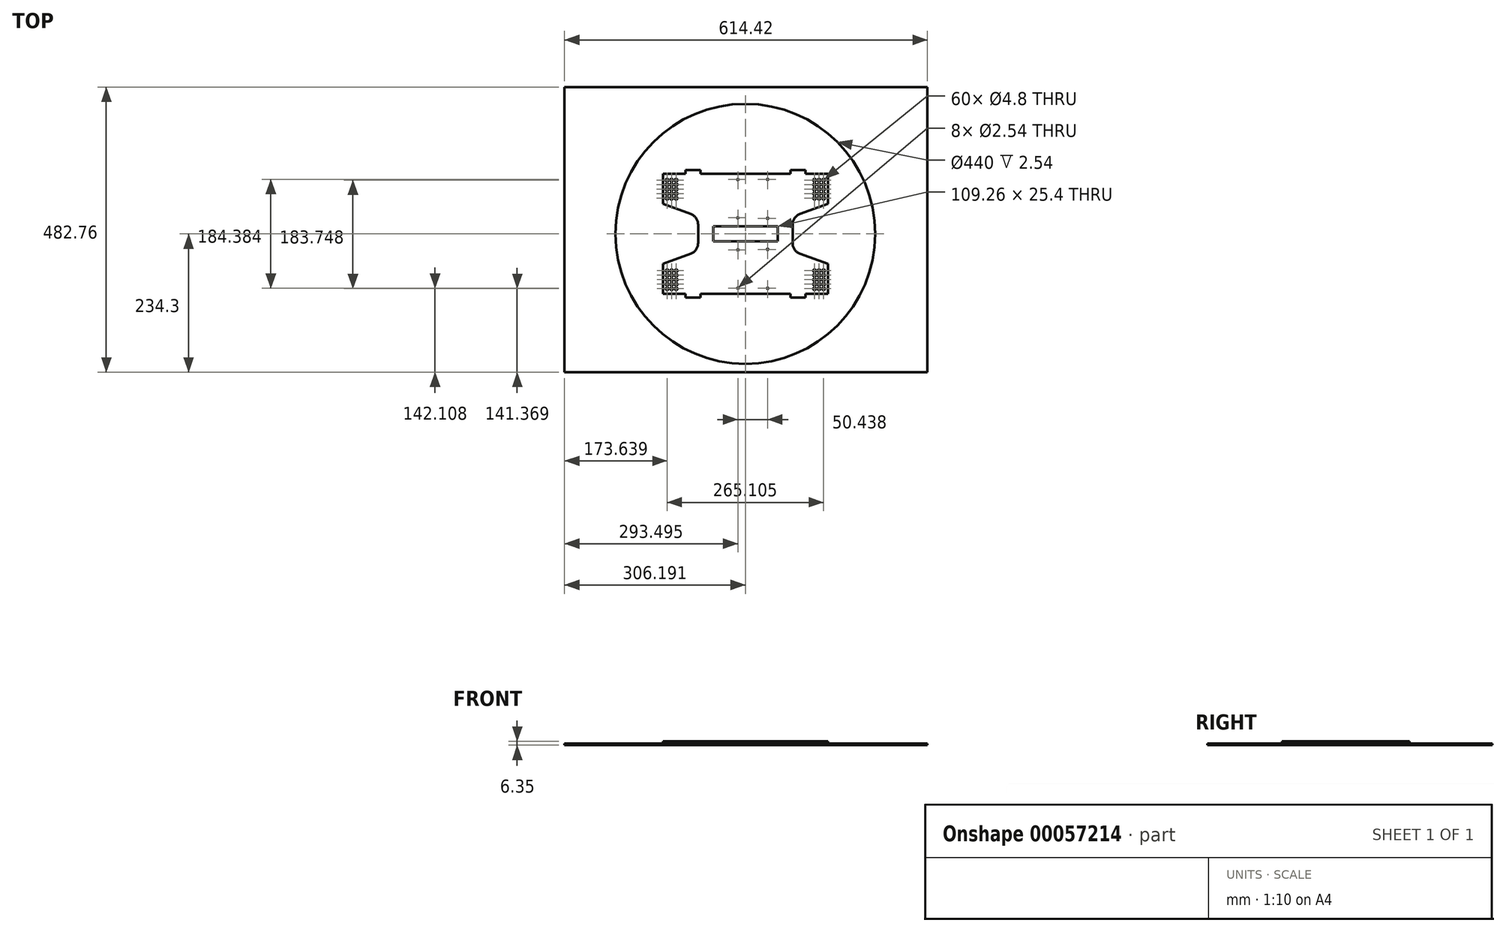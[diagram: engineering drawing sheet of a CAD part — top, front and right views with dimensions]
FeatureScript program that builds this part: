
annotation { "Feature Type Name" : "Feature", "Feature Type Description" : "" }
export const myFeature = defineFeature(function(context is Context, id is Id, definition is map)
    precondition{}
    {
        {
            var Q0;
            Q0=qCreatedBy(makeId("Top.planeOp"),FACE);
            var sketch = newSketch(context, id + "F0", { "sketchPlane" : qUnion([Q0])});
            skCircle(sketch, "E0", {"center": v(3.84, 0) * mm, "radius": 220 * mm});
            skLineSegment(sketch, "E1.bottom", {"start": v(-302.35, 248.46) * mm, "end": v(312.07, 248.46) * mm});
            skLineSegment(sketch, "E1.top", {"start": v(-302.35, -234.3) * mm, "end": v(312.07, -234.3) * mm});
            skLineSegment(sketch, "E1.left", {"start": v(-302.35, 248.46) * mm, "end": v(-302.35, -234.3) * mm});
            skLineSegment(sketch, "E1.right", {"start": v(312.07, 248.46) * mm, "end": v(312.07, -234.3) * mm});
            skSolve(sketch);
        }
        {
            var Q0;
            Q0=makeQuery(id+"F0.imprint","IMPRINT",FACE,{"disambiguationData":[TD([[makeQuery(id+"F0.imprint","IMPRINT",EDGE,{"derivedFrom":sQuery(id+"F0.wireOp",EDGE,"E0")}),1.0]])]});
            var sketch = newSketch(context, id + "F1", { "sketchPlane" : qUnion([Q0])});
            skLineSegment(sketch, "E2.bottom", {"start": v(-135.86, 101.6) * mm, "end": v(143.54, 101.6) * mm});
            skLineSegment(sketch, "E2.top", {"start": v(-135.86, -101.6) * mm, "end": v(143.54, -101.6) * mm});
            skLineSegment(sketch, "E2.left", {"start": v(-135.86, 101.6) * mm, "end": v(-135.86, -101.6) * mm});
            skLineSegment(sketch, "E2.right", {"start": v(143.54, 101.6) * mm, "end": v(143.54, -101.6) * mm});
            skLineSegment(sketch, "E3.bottom", {"start": v(-97.76, -101.6) * mm, "end": v(-72.36, -101.6) * mm});
            skLineSegment(sketch, "E3.top", {"start": v(-97.76, -107.95) * mm, "end": v(-72.36, -107.95) * mm});
            skLineSegment(sketch, "E3.left", {"start": v(-97.76, -101.6) * mm, "end": v(-97.76, -107.95) * mm});
            skLineSegment(sketch, "E3.right", {"start": v(-72.36, -101.6) * mm, "end": v(-72.36, -107.95) * mm});
            skLineSegment(sketch, "E4.bottom", {"start": v(105.44, -101.6) * mm, "end": v(80.04, -101.6) * mm});
            skLineSegment(sketch, "E4.top", {"start": v(105.44, -107.95) * mm, "end": v(80.04, -107.95) * mm});
            skLineSegment(sketch, "E4.left", {"start": v(105.44, -101.6) * mm, "end": v(105.44, -107.95) * mm});
            skLineSegment(sketch, "E4.right", {"start": v(80.04, -101.6) * mm, "end": v(80.04, -107.95) * mm});
            skLineSegment(sketch, "E5.MirrorCS", {"start": v(-97.76, 107.95) * mm, "end": v(-72.36, 107.95) * mm});
            skLineSegment(sketch, "E6.MirrorCS", {"start": v(-97.76, 101.6) * mm, "end": v(-72.36, 101.6) * mm});
            skLineSegment(sketch, "E7.MirrorCS", {"start": v(-97.76, 101.6) * mm, "end": v(-97.76, 107.95) * mm});
            skLineSegment(sketch, "E8.MirrorCS", {"start": v(-72.36, 101.6) * mm, "end": v(-72.36, 107.95) * mm});
            skLineSegment(sketch, "E9.MirrorCS", {"start": v(80.04, 101.6) * mm, "end": v(80.04, 107.95) * mm});
            skLineSegment(sketch, "E10.MirrorCS", {"start": v(105.44, 101.6) * mm, "end": v(105.44, 107.95) * mm});
            skLineSegment(sketch, "E11.MirrorCS", {"start": v(105.44, 107.95) * mm, "end": v(80.04, 107.95) * mm});
            skLineSegment(sketch, "E12.MirrorCS", {"start": v(105.44, 101.6) * mm, "end": v(80.04, 101.6) * mm});
            skLineSegment(sketch, "E13", {"start": v(95.83, 33.4) * mm, "end": v(143.54, 50.85) * mm});
            skLineSegment(sketch, "E14", {"start": v(95.78, -33.63) * mm, "end": v(95.83, 33.4) * mm});
            skLineSegment(sketch, "E15", {"start": v(143.54, -51.02) * mm, "end": v(95.78, -33.63) * mm});
            skLineSegment(sketch, "E16", {"start": v(-88.2, 33.27) * mm, "end": v(-135.86, 51.37) * mm});
            skLineSegment(sketch, "E17", {"start": v(-88.14, -33.49) * mm, "end": v(-88.2, 33.27) * mm});
            skLineSegment(sketch, "E18", {"start": v(-88.14, -33.49) * mm, "end": v(-135.86, -51.13) * mm});
            skSolve(sketch);
        }
        {
            var Q0;
            Q0=qSketchRegion(id+"F1",true);
            extrude(context, id + "F2", {"entities" : qUnion([Q0]), "depth" : 6.35 * mm});
        }
        {
            var Q0;
            Q0=makeQuery(id+"F0.imprint","IMPRINT",FACE,{"disambiguationData":[TD([[makeQuery(id+"F0.imprint","IMPRINT",EDGE,{"derivedFrom":sQuery(id+"F0.wireOp",EDGE,"E0")}),-1.0]])]});
            extrude(context, id + "F3", {"entities" : qUnion([Q0]), "depth" : 2.54 * mm});
        }
        {
            var Q0;
            Q0=makeQuery(id+"F2.opExtrude","CAP_FACE",FACE,{"disambiguationData":[OSD([sQuery(id+"F1.wireOp",EDGE,"E2.bottom"),sQuery(id+"F1.wireOp",EDGE,"E2.top"),sQuery(id+"F1.wireOp",EDGE,"E2.left"),sQuery(id+"F1.wireOp",EDGE,"E2.right"),sQuery(id+"F1.wireOp",EDGE,"E3.top"),sQuery(id+"F1.wireOp",EDGE,"E3.left"),sQuery(id+"F1.wireOp",EDGE,"E3.right"),sQuery(id+"F1.wireOp",EDGE,"E4.top"),sQuery(id+"F1.wireOp",EDGE,"E4.left"),sQuery(id+"F1.wireOp",EDGE,"E4.right"),sQuery(id+"F1.wireOp",EDGE,"E5.MirrorCS"),sQuery(id+"F1.wireOp",EDGE,"E7.MirrorCS"),sQuery(id+"F1.wireOp",EDGE,"E8.MirrorCS"),sQuery(id+"F1.wireOp",EDGE,"E9.MirrorCS"),sQuery(id+"F1.wireOp",EDGE,"E10.MirrorCS"),sQuery(id+"F1.wireOp",EDGE,"E11.MirrorCS")])],"isStart":false});
            var sketch = newSketch(context, id + "F4", { "sketchPlane" : qUnion([Q0])});
            skLineSegment(sketch, "E19", {"start": v(143.54, 50.8) * mm, "end": v(96.4, 33.64) * mm});
            skLineSegment(sketch, "E20", {"start": v(143.54, -50.8) * mm, "end": v(96.4, -33.64) * mm});
            skLineSegment(sketch, "E21", {"start": v(83.87, -15.74) * mm, "end": v(83.87, 15.74) * mm});
            skLineSegment(sketch, "E22", {"start": v(-135.86, 50.8) * mm, "end": v(-88.72, 33.64) * mm});
            skLineSegment(sketch, "E23", {"start": v(-135.86, -50.8) * mm, "end": v(-88.72, -33.64) * mm});
            skLineSegment(sketch, "E24", {"start": v(-76.19, 15.74) * mm, "end": v(-76.19, -15.74) * mm});
            skPoint(sketch, "E25.visualSharp", {"position": v(-76.19, 29.08) * mm});
            skArc(sketch, "E25.filletArc", {"start": v(-76.19, 15.74) * mm, "mid": v(-79.63, 26.67) * mm, "end": v(-88.72, 33.64) * mm});
            skPoint(sketch, "E26.visualSharp", {"position": v(-76.19, -29.08) * mm});
            skArc(sketch, "E26.filletArc", {"start": v(-88.72, -33.64) * mm, "mid": v(-79.63, -26.67) * mm, "end": v(-76.19, -15.74) * mm});
            skPoint(sketch, "E27.visualSharp", {"position": v(83.87, 29.08) * mm});
            skArc(sketch, "E27.filletArc", {"start": v(96.4, 33.64) * mm, "mid": v(87.32, 26.67) * mm, "end": v(83.87, 15.74) * mm});
            skPoint(sketch, "E28.visualSharp", {"position": v(83.87, -29.08) * mm});
            skArc(sketch, "E28.filletArc", {"start": v(83.87, -15.74) * mm, "mid": v(87.32, -26.67) * mm, "end": v(96.4, -33.64) * mm});
            skSolve(sketch);
        }
        {
            var Q0;
            {var subQ2=sQuery(id+"F4.wireOp",EDGE,"E19");Q0=makeQuery(id+"F4.imprint","IMPRINT",FACE,{"disambiguationData":[TD([[makeQuery(id+"F4.imprint","IMPRINT",EDGE,{"derivedFrom":subQ2}),1.0]])]});}
            var Q1;
            {var subQ2=sQuery(id+"F4.wireOp",EDGE,"E22");Q1=makeQuery(id+"F4.imprint","IMPRINT",FACE,{"disambiguationData":[TD([[makeQuery(id+"F4.imprint","IMPRINT",EDGE,{"derivedFrom":subQ2}),-1.0]])]});}
            extrude(context, id + "F5", {"entities" : qUnion([Q0, Q1]), "operationType" : NewBodyOperationType.REMOVE, "oppositeDirection" : true, "depth" : 25.4 * mm});
        }
        {
            var Q0;
            Q0=makeQuery(id+"F2.opExtrude","CAP_FACE",FACE,{"disambiguationData":[OSD([sQuery(id+"F1.wireOp",EDGE,"E2.bottom"),sQuery(id+"F1.wireOp",EDGE,"E2.top"),sQuery(id+"F1.wireOp",EDGE,"E2.left"),sQuery(id+"F1.wireOp",EDGE,"E2.right"),sQuery(id+"F1.wireOp",EDGE,"E3.top"),sQuery(id+"F1.wireOp",EDGE,"E3.left"),sQuery(id+"F1.wireOp",EDGE,"E3.right"),sQuery(id+"F1.wireOp",EDGE,"E4.top"),sQuery(id+"F1.wireOp",EDGE,"E4.left"),sQuery(id+"F1.wireOp",EDGE,"E4.right"),sQuery(id+"F1.wireOp",EDGE,"E5.MirrorCS"),sQuery(id+"F1.wireOp",EDGE,"E7.MirrorCS"),sQuery(id+"F1.wireOp",EDGE,"E8.MirrorCS"),sQuery(id+"F1.wireOp",EDGE,"E9.MirrorCS"),sQuery(id+"F1.wireOp",EDGE,"E10.MirrorCS"),sQuery(id+"F1.wireOp",EDGE,"E11.MirrorCS")])],"isStart":false});
            var sketch = newSketch(context, id + "F6", { "sketchPlane" : qUnion([Q0])});
            skCircle(sketch, "E29", {"center": v(-128.71, 90.82) * mm, "radius": 2.4 * mm});
            skCircle(sketch, "E30.0.1.0", {"center": v(-128.71, 83.2) * mm, "radius": 2.4 * mm});
            skCircle(sketch, "E30.0.2.0", {"center": v(-128.71, 75.58) * mm, "radius": 2.4 * mm});
            skCircle(sketch, "E30.0.3.0", {"center": v(-128.71, 67.96) * mm, "radius": 2.4 * mm});
            skCircle(sketch, "E30.0.4.0", {"center": v(-128.71, 60.34) * mm, "radius": 2.4 * mm});
            skCircle(sketch, "E30.1.0.0", {"center": v(-121.1, 90.82) * mm, "radius": 2.4 * mm});
            skCircle(sketch, "E30.1.1.0", {"center": v(-121.1, 83.2) * mm, "radius": 2.4 * mm});
            skCircle(sketch, "E30.1.2.0", {"center": v(-121.1, 75.58) * mm, "radius": 2.4 * mm});
            skCircle(sketch, "E30.1.3.0", {"center": v(-121.1, 67.96) * mm, "radius": 2.4 * mm});
            skCircle(sketch, "E30.1.4.0", {"center": v(-121.1, 60.34) * mm, "radius": 2.4 * mm});
            skCircle(sketch, "E30.2.0.0", {"center": v(-113.47, 90.82) * mm, "radius": 2.4 * mm});
            skCircle(sketch, "E30.2.1.0", {"center": v(-113.47, 83.2) * mm, "radius": 2.4 * mm});
            skCircle(sketch, "E30.2.2.0", {"center": v(-113.47, 75.58) * mm, "radius": 2.4 * mm});
            skCircle(sketch, "E30.2.3.0", {"center": v(-113.47, 67.96) * mm, "radius": 2.4 * mm});
            skCircle(sketch, "E30.2.4.0", {"center": v(-113.47, 60.34) * mm, "radius": 2.4 * mm});
            skLineSegment(sketch, "E30.direction1", {"start": v(-128.71, 90.82) * mm, "end": v(-121.1, 90.82) * mm, "construction": true});
            skLineSegment(sketch, "E30.direction2", {"start": v(-128.71, 90.82) * mm, "end": v(-128.71, 83.2) * mm, "construction": true});
            skLineSegment(sketch, "E31.direction1", {"start": v(-128.6, -62.45) * mm, "end": v(-120.98, -62.45) * mm, "construction": true});
            skCircle(sketch, "E31.2.0.0", {"center": v(-113.36, -62.45) * mm, "radius": 2.4 * mm});
            skCircle(sketch, "E31.1.4.0", {"center": v(-120.98, -92.93) * mm, "radius": 2.4 * mm});
            skCircle(sketch, "E31.1.3.0", {"center": v(-120.98, -85.31) * mm, "radius": 2.4 * mm});
            skCircle(sketch, "E31.0.4.0", {"center": v(-128.6, -92.93) * mm, "radius": 2.4 * mm});
            skCircle(sketch, "E31.1.2.0", {"center": v(-120.98, -77.7) * mm, "radius": 2.4 * mm});
            skCircle(sketch, "E31.2.3.0", {"center": v(-113.36, -85.31) * mm, "radius": 2.4 * mm});
            skCircle(sketch, "E31.2.2.0", {"center": v(-113.36, -77.7) * mm, "radius": 2.4 * mm});
            skCircle(sketch, "E31.1.1.0", {"center": v(-120.98, -70.07) * mm, "radius": 2.4 * mm});
            skCircle(sketch, "E31.0.3.0", {"center": v(-128.6, -85.31) * mm, "radius": 2.4 * mm});
            skCircle(sketch, "E31.0.2.0", {"center": v(-128.6, -77.7) * mm, "radius": 2.4 * mm});
            skCircle(sketch, "E31.2.1.0", {"center": v(-113.36, -70.07) * mm, "radius": 2.4 * mm});
            skCircle(sketch, "E31.2.4.0", {"center": v(-113.36, -92.93) * mm, "radius": 2.4 * mm});
            skLineSegment(sketch, "E31.direction2", {"start": v(-128.6, -62.45) * mm, "end": v(-128.6, -70.07) * mm, "construction": true});
            skCircle(sketch, "E31.1.0.0", {"center": v(-120.98, -62.45) * mm, "radius": 2.4 * mm});
            skCircle(sketch, "E31.0.1.0", {"center": v(-128.6, -70.07) * mm, "radius": 2.4 * mm});
            skCircle(sketch, "E32", {"center": v(-128.6, -62.45) * mm, "radius": 2.4 * mm});
            skLineSegment(sketch, "E33", {"start": v(3.84, 72.78) * mm, "end": v(3.84, -50.53) * mm});
            skCircle(sketch, "E34.MirrorC", {"center": v(121.15, 60.34) * mm, "radius": 2.4 * mm});
            skCircle(sketch, "E35.MirrorC", {"center": v(128.77, 60.34) * mm, "radius": 2.4 * mm});
            skCircle(sketch, "E36.MirrorC", {"center": v(136.4, 60.34) * mm, "radius": 2.4 * mm});
            skCircle(sketch, "E37.MirrorC", {"center": v(136.4, 67.96) * mm, "radius": 2.4 * mm});
            skCircle(sketch, "E38.MirrorC", {"center": v(128.77, 67.96) * mm, "radius": 2.4 * mm});
            skCircle(sketch, "E39.MirrorC", {"center": v(121.15, 67.96) * mm, "radius": 2.4 * mm});
            skCircle(sketch, "E40.MirrorC", {"center": v(121.15, 75.58) * mm, "radius": 2.4 * mm});
            skCircle(sketch, "E41.MirrorC", {"center": v(128.77, 75.58) * mm, "radius": 2.4 * mm});
            skCircle(sketch, "E42.MirrorC", {"center": v(136.4, 75.58) * mm, "radius": 2.4 * mm});
            skCircle(sketch, "E43.MirrorC", {"center": v(136.4, 83.2) * mm, "radius": 2.4 * mm});
            skCircle(sketch, "E44.MirrorC", {"center": v(128.77, 83.2) * mm, "radius": 2.4 * mm});
            skCircle(sketch, "E45.MirrorC", {"center": v(128.77, 90.82) * mm, "radius": 2.4 * mm});
            skCircle(sketch, "E46.MirrorC", {"center": v(136.4, 90.82) * mm, "radius": 2.4 * mm});
            skCircle(sketch, "E47.MirrorC", {"center": v(121.15, 90.82) * mm, "radius": 2.4 * mm});
            skCircle(sketch, "E48.MirrorC", {"center": v(121.15, 83.2) * mm, "radius": 2.4 * mm});
            skCircle(sketch, "E49.MirrorC", {"center": v(136.29, -62.45) * mm, "radius": 2.4 * mm});
            skCircle(sketch, "E50.MirrorC", {"center": v(136.29, -70.07) * mm, "radius": 2.4 * mm});
            skCircle(sketch, "E51.MirrorC", {"center": v(136.29, -77.7) * mm, "radius": 2.4 * mm});
            skCircle(sketch, "E52.MirrorC", {"center": v(136.29, -85.31) * mm, "radius": 2.4 * mm});
            skCircle(sketch, "E53.MirrorC", {"center": v(136.29, -92.93) * mm, "radius": 2.4 * mm});
            skCircle(sketch, "E54.MirrorC", {"center": v(128.67, -92.93) * mm, "radius": 2.4 * mm});
            skCircle(sketch, "E55.MirrorC", {"center": v(128.67, -85.31) * mm, "radius": 2.4 * mm});
            skCircle(sketch, "E56.MirrorC", {"center": v(128.67, -77.7) * mm, "radius": 2.4 * mm});
            skCircle(sketch, "E57.MirrorC", {"center": v(128.67, -70.07) * mm, "radius": 2.4 * mm});
            skCircle(sketch, "E58.MirrorC", {"center": v(128.67, -62.45) * mm, "radius": 2.4 * mm});
            skCircle(sketch, "E59.MirrorC", {"center": v(121.05, -62.45) * mm, "radius": 2.4 * mm});
            skCircle(sketch, "E60.MirrorC", {"center": v(121.05, -70.07) * mm, "radius": 2.4 * mm});
            skCircle(sketch, "E61.MirrorC", {"center": v(121.05, -77.7) * mm, "radius": 2.4 * mm});
            skCircle(sketch, "E62.MirrorC", {"center": v(121.05, -85.31) * mm, "radius": 2.4 * mm});
            skCircle(sketch, "E63.MirrorC", {"center": v(121.05, -92.93) * mm, "radius": 2.4 * mm});
            skSolve(sketch);
        }
        {
            var Q0;
            Q0=qSketchRegion(id+"F6",true);
            extrude(context, id + "F7", {"entities" : qUnion([Q0]), "operationType" : NewBodyOperationType.REMOVE, "oppositeDirection" : true, "depth" : 25.4 * mm});
        }
        {
            var Q0;
            Q0=makeQuery(id+"F2.opExtrude","CAP_FACE",FACE,{"disambiguationData":[OSD([sQuery(id+"F1.wireOp",EDGE,"E2.bottom"),sQuery(id+"F1.wireOp",EDGE,"E2.top"),sQuery(id+"F1.wireOp",EDGE,"E2.left"),sQuery(id+"F1.wireOp",EDGE,"E2.right"),sQuery(id+"F1.wireOp",EDGE,"E3.top"),sQuery(id+"F1.wireOp",EDGE,"E3.left"),sQuery(id+"F1.wireOp",EDGE,"E3.right"),sQuery(id+"F1.wireOp",EDGE,"E4.top"),sQuery(id+"F1.wireOp",EDGE,"E4.left"),sQuery(id+"F1.wireOp",EDGE,"E4.right"),sQuery(id+"F1.wireOp",EDGE,"E5.MirrorCS"),sQuery(id+"F1.wireOp",EDGE,"E7.MirrorCS"),sQuery(id+"F1.wireOp",EDGE,"E8.MirrorCS"),sQuery(id+"F1.wireOp",EDGE,"E9.MirrorCS"),sQuery(id+"F1.wireOp",EDGE,"E10.MirrorCS"),sQuery(id+"F1.wireOp",EDGE,"E11.MirrorCS")])],"isStart":false});
            var sketch = newSketch(context, id + "F8", { "sketchPlane" : qUnion([Q0])});
            skLineSegment(sketch, "E64.bottom", {"start": v(-50.79, 12.7) * mm, "end": v(58.47, 12.7) * mm});
            skLineSegment(sketch, "E64.top", {"start": v(-50.79, -12.7) * mm, "end": v(58.47, -12.7) * mm});
            skLineSegment(sketch, "E64.left", {"start": v(-50.79, 12.7) * mm, "end": v(-50.79, -12.7) * mm});
            skLineSegment(sketch, "E64.right", {"start": v(58.47, 12.7) * mm, "end": v(58.47, -12.7) * mm});
            skSolve(sketch);
        }
        {
            var Q0;
            Q0=qSketchRegion(id+"F8",true);
            extrude(context, id + "F9", {"entities" : qUnion([Q0]), "operationType" : NewBodyOperationType.REMOVE, "oppositeDirection" : true, "depth" : 25.4 * mm});
        }
        {
            var Q0;
            Q0=makeQuery(id+"F2.opExtrude","CAP_FACE",FACE,{"disambiguationData":[OSD([sQuery(id+"F1.wireOp",EDGE,"E2.bottom"),sQuery(id+"F1.wireOp",EDGE,"E2.top"),sQuery(id+"F1.wireOp",EDGE,"E2.left"),sQuery(id+"F1.wireOp",EDGE,"E2.right"),sQuery(id+"F1.wireOp",EDGE,"E3.top"),sQuery(id+"F1.wireOp",EDGE,"E3.left"),sQuery(id+"F1.wireOp",EDGE,"E3.right"),sQuery(id+"F1.wireOp",EDGE,"E4.top"),sQuery(id+"F1.wireOp",EDGE,"E4.left"),sQuery(id+"F1.wireOp",EDGE,"E4.right"),sQuery(id+"F1.wireOp",EDGE,"E5.MirrorCS"),sQuery(id+"F1.wireOp",EDGE,"E7.MirrorCS"),sQuery(id+"F1.wireOp",EDGE,"E8.MirrorCS"),sQuery(id+"F1.wireOp",EDGE,"E9.MirrorCS"),sQuery(id+"F1.wireOp",EDGE,"E10.MirrorCS"),sQuery(id+"F1.wireOp",EDGE,"E11.MirrorCS")])],"isStart":false});
            var sketch = newSketch(context, id + "F10", { "sketchPlane" : qUnion([Q0])});
            skCircle(sketch, "E65", {"center": v(41.58, -92.2) * mm, "radius": 1.27 * mm});
            skCircle(sketch, "E66", {"center": v(41.58, -26.27) * mm, "radius": 1.27 * mm});
            skLineSegment(sketch, "E67", {"start": v(41.58, -92.2) * mm, "end": v(41.58, -17.04) * mm});
            skLineSegment(sketch, "E68", {"start": v(-8.85, -91.88) * mm, "end": v(-8.85, -17.04) * mm});
            skCircle(sketch, "E69", {"center": v(-8.85, -27.1) * mm, "radius": 1.27 * mm});
            skCircle(sketch, "E70", {"center": v(-8.85, -91.88) * mm, "radius": 1.27 * mm});
            skLineSegment(sketch, "E71", {"start": v(41.58, -17.04) * mm, "end": v(-22.87, -17.04) * mm});
            skLineSegment(sketch, "E72.MirrorCS", {"start": v(41.58, 17.04) * mm, "end": v(-22.87, 17.04) * mm});
            skLineSegment(sketch, "E73.MirrorCS", {"start": v(-8.85, 91.88) * mm, "end": v(-8.85, 17.04) * mm});
            skLineSegment(sketch, "E74.MirrorCS", {"start": v(41.58, 92.2) * mm, "end": v(41.58, 17.04) * mm});
            skCircle(sketch, "E75.MirrorC", {"center": v(-8.85, 27.1) * mm, "radius": 1.27 * mm});
            skCircle(sketch, "E76.MirrorC", {"center": v(41.58, 26.27) * mm, "radius": 1.27 * mm});
            skCircle(sketch, "E77.MirrorC", {"center": v(41.58, 92.2) * mm, "radius": 1.27 * mm});
            skCircle(sketch, "E78.MirrorC", {"center": v(-8.85, 91.88) * mm, "radius": 1.27 * mm});
            skSolve(sketch);
        }
        {
            var Q0;
            Q0=qSketchRegion(id+"F10",true);
            extrude(context, id + "F11", {"entities" : qUnion([Q0]), "operationType" : NewBodyOperationType.REMOVE, "oppositeDirection" : true, "depth" : 50.8 * mm});
        }
    });
